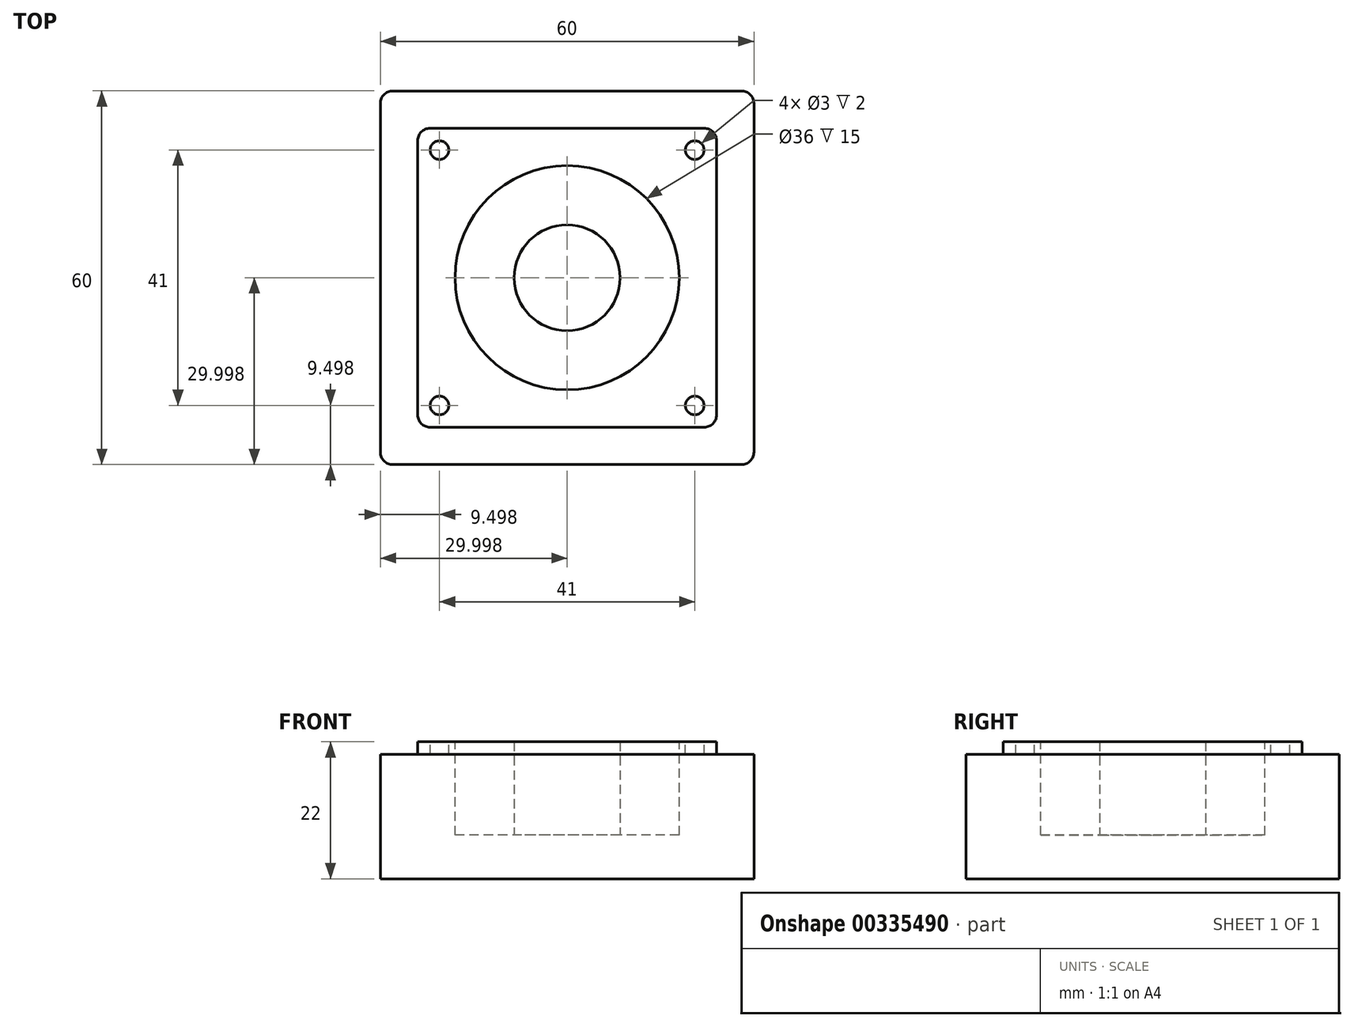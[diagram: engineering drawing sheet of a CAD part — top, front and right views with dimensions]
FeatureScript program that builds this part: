
annotation { "Feature Type Name" : "Feature", "Feature Type Description" : "" }
export const myFeature = defineFeature(function(context is Context, id is Id, definition is map)
    precondition{}
    {
        {
            var Q0;
            Q0=qCreatedBy(makeId("Top.planeOp"),FACE);
            var sketch = newSketch(context, id + "F0", { "sketchPlane" : qUnion([Q0])});
            skLineSegment(sketch, "E0.bottom", {"start": v(-15, 60.74) * mm, "end": v(45, 60.74) * mm});
            skLineSegment(sketch, "E0.top", {"start": v(-15, 0.74) * mm, "end": v(45, 0.74) * mm});
            skLineSegment(sketch, "E0.left", {"start": v(-15, 60.74) * mm, "end": v(-15, 0.74) * mm});
            skLineSegment(sketch, "E0.right", {"start": v(45, 60.74) * mm, "end": v(45, 0.74) * mm});
            skSolve(sketch);
        }
        {
            var Q0;
            Q0 = qSketchRegion(id + "F0", true);
            extrude(context, id + "F1", {"entities" : qUnion([Q0]), "depth" : 20 * mm});
        }
        {
            var Q0;
            Q0=makeQuery(id+"F1.opExtrude","CAP_FACE",FACE,{"disambiguationData":[OSD([sQuery(id+"F0.wireOp",EDGE,"E0.bottom"),sQuery(id+"F0.wireOp",EDGE,"E0.top"),sQuery(id+"F0.wireOp",EDGE,"E0.left"),sQuery(id+"F0.wireOp",EDGE,"E0.right")])],"isStart":false});
            var sketch = newSketch(context, id + "F2", { "sketchPlane" : qUnion([Q0])});
            skLineSegment(sketch, "E1.0", {"start": v(-9, 54.74) * mm, "end": v(-9, 6.74) * mm});
            skLineSegment(sketch, "E1.1", {"start": v(39, 54.74) * mm, "end": v(-9, 54.74) * mm});
            skLineSegment(sketch, "E1.2", {"start": v(39, 6.74) * mm, "end": v(39, 54.74) * mm});
            skLineSegment(sketch, "E1.3", {"start": v(-9, 6.74) * mm, "end": v(39, 6.74) * mm});
            skSolve(sketch);
        }
        {
            var Q0;
            Q0=makeQuery(id+"F2.imprint","IMPRINT",FACE,{"disambiguationData":[TD([[makeQuery(id+"F2.imprint","IMPRINT",EDGE,{"derivedFrom":sQuery(id+"F2.wireOp",EDGE,"E1.0")}),1.0]])]});
            extrude(context, id + "F3", {"entities" : qUnion([Q0]), "operationType" : NewBodyOperationType.ADD, "depth" : 2 * mm});
        }
        {
            var Q0;
            Q0=makeQuery(id+"F3.opExtrude","CAP_FACE",FACE,{"disambiguationData":[OSD([sQuery(id+"F2.wireOp",EDGE,"E1.0"),sQuery(id+"F2.wireOp",EDGE,"E1.1"),sQuery(id+"F2.wireOp",EDGE,"E1.2"),sQuery(id+"F2.wireOp",EDGE,"E1.3")])],"isStart":false});
            var sketch = newSketch(context, id + "F4", { "sketchPlane" : qUnion([Q0])});
            skLineSegment(sketch, "E2.0", {"start": v(-5.5, 51.24) * mm, "end": v(-5.5, 10.24) * mm});
            skLineSegment(sketch, "E2.1", {"start": v(35.5, 51.24) * mm, "end": v(-5.5, 51.24) * mm});
            skLineSegment(sketch, "E2.2", {"start": v(35.5, 10.24) * mm, "end": v(35.5, 51.24) * mm});
            skLineSegment(sketch, "E2.3", {"start": v(-5.5, 10.24) * mm, "end": v(35.5, 10.24) * mm});
            skCircle(sketch, "E3", {"center": v(-5.5, 51.24) * mm, "radius": 1.5 * mm});
            skCircle(sketch, "E4", {"center": v(35.5, 51.24) * mm, "radius": 1.5 * mm});
            skCircle(sketch, "E5", {"center": v(35.5, 10.24) * mm, "radius": 1.5 * mm});
            skCircle(sketch, "E6", {"center": v(-5.5, 10.24) * mm, "radius": 1.5 * mm});
            skSolve(sketch);
        }
        {
            var Q0;
            {var subQ0=sQuery(id+"F4.wireOp",EDGE,"E2.1");var subQ1=sQuery(id+"F4.wireOp",EDGE,"E2.0");var subQ2=makeQuery(id+"F4.imprint","INTERSECT",VERTEX,{"derivedFrom":[subQ1,subQ0]});Q0=makeQuery(id+"F4.imprint","IMPRINT",FACE,{"disambiguationData":[TD([[makeQuery(id+"F4.imprint","IMPRINT",EDGE,{"disambiguationData":[TD([[subQ2,-1.0]])],"derivedFrom":subQ1}),-1.0]])]});}
            var Q1;
            {var subQ0=sQuery(id+"F4.wireOp",EDGE,"E2.1");var subQ1=sQuery(id+"F4.wireOp",EDGE,"E2.0");var subQ2=makeQuery(id+"F4.imprint","INTERSECT",VERTEX,{"derivedFrom":[subQ1,subQ0]});Q1=makeQuery(id+"F4.imprint","IMPRINT",FACE,{"disambiguationData":[TD([[makeQuery(id+"F4.imprint","IMPRINT",EDGE,{"disambiguationData":[TD([[subQ2,-1.0]])],"derivedFrom":subQ1}),1.0]])]});}
            var Q2;
            {var subQ0=sQuery(id+"F4.wireOp",EDGE,"E2.2");var subQ1=sQuery(id+"F4.wireOp",EDGE,"E2.1");var subQ2=makeQuery(id+"F4.imprint","INTERSECT",VERTEX,{"derivedFrom":[subQ1,subQ0]});Q2=makeQuery(id+"F4.imprint","IMPRINT",FACE,{"disambiguationData":[TD([[makeQuery(id+"F4.imprint","IMPRINT",EDGE,{"disambiguationData":[TD([[subQ2,-1.0]])],"derivedFrom":subQ1}),1.0]])]});}
            var Q3;
            {var subQ0=sQuery(id+"F4.wireOp",EDGE,"E2.3");var subQ1=sQuery(id+"F4.wireOp",EDGE,"E2.2");var subQ2=makeQuery(id+"F4.imprint","INTERSECT",VERTEX,{"derivedFrom":[subQ1,subQ0]});Q3=makeQuery(id+"F4.imprint","IMPRINT",FACE,{"disambiguationData":[TD([[makeQuery(id+"F4.imprint","IMPRINT",EDGE,{"disambiguationData":[TD([[subQ2,-1.0]])],"derivedFrom":subQ1}),1.0]])]});}
            var Q4;
            {var subQ0=sQuery(id+"F4.wireOp",EDGE,"E2.3");var subQ1=sQuery(id+"F4.wireOp",EDGE,"E2.0");var subQ2=makeQuery(id+"F4.imprint","INTERSECT",VERTEX,{"derivedFrom":[subQ1,subQ0]});Q4=makeQuery(id+"F4.imprint","IMPRINT",FACE,{"disambiguationData":[TD([[makeQuery(id+"F4.imprint","IMPRINT",EDGE,{"disambiguationData":[TD([[subQ2,1.0]])],"derivedFrom":subQ1}),1.0]])]});}
            var Q5;
            {var subQ0=sQuery(id+"F4.wireOp",EDGE,"E2.3");var subQ1=sQuery(id+"F4.wireOp",EDGE,"E2.0");var subQ2=makeQuery(id+"F4.imprint","INTERSECT",VERTEX,{"derivedFrom":[subQ1,subQ0]});Q5=makeQuery(id+"F4.imprint","IMPRINT",FACE,{"disambiguationData":[TD([[makeQuery(id+"F4.imprint","IMPRINT",EDGE,{"disambiguationData":[TD([[subQ2,1.0]])],"derivedFrom":subQ1}),-1.0]])]});}
            var Q6;
            {var subQ0=sQuery(id+"F4.wireOp",EDGE,"E2.3");var subQ1=sQuery(id+"F4.wireOp",EDGE,"E2.2");var subQ2=makeQuery(id+"F4.imprint","INTERSECT",VERTEX,{"derivedFrom":[subQ1,subQ0]});Q6=makeQuery(id+"F4.imprint","IMPRINT",FACE,{"disambiguationData":[TD([[makeQuery(id+"F4.imprint","IMPRINT",EDGE,{"disambiguationData":[TD([[subQ2,-1.0]])],"derivedFrom":subQ1}),-1.0]])]});}
            var Q7;
            {var subQ0=sQuery(id+"F4.wireOp",EDGE,"E2.2");var subQ1=sQuery(id+"F4.wireOp",EDGE,"E2.1");var subQ2=makeQuery(id+"F4.imprint","INTERSECT",VERTEX,{"derivedFrom":[subQ1,subQ0]});Q7=makeQuery(id+"F4.imprint","IMPRINT",FACE,{"disambiguationData":[TD([[makeQuery(id+"F4.imprint","IMPRINT",EDGE,{"disambiguationData":[TD([[subQ2,-1.0]])],"derivedFrom":subQ1}),-1.0]])]});}
            extrude(context, id + "F5", {"entities" : qUnion([Q0, Q1, Q2, Q3, Q4, Q5, Q6, Q7]), "operationType" : NewBodyOperationType.REMOVE, "oppositeDirection" : true, "depth" : 2 * mm});
        }
        {
            var Q0;
            Q0=makeQuery(id+"F3.opExtrude","CAP_FACE",FACE,{"disambiguationData":[OSD([sQuery(id+"F2.wireOp",EDGE,"E1.0"),sQuery(id+"F2.wireOp",EDGE,"E1.1"),sQuery(id+"F2.wireOp",EDGE,"E1.2"),sQuery(id+"F2.wireOp",EDGE,"E1.3")])],"isStart":false});
            var sketch = newSketch(context, id + "F6", { "sketchPlane" : qUnion([Q0])});
            skCircle(sketch, "E7", {"center": v(15, 30.74) * mm, "radius": 18 * mm});
            skPoint(sketch, "E7.centerSnap0", {"position": v(39, 30.74) * mm});
            skPoint(sketch, "E7.centerSnap1", {"position": v(15, 54.74) * mm});
            skSolve(sketch);
        }
        {
            var Q0;
            Q0=makeQuery(id+"F6.imprint","IMPRINT",FACE,{"disambiguationData":[TD([[makeQuery(id+"F6.imprint","IMPRINT",EDGE,{"derivedFrom":sQuery(id+"F6.wireOp",EDGE,"E7")}),1.0]])]});
            extrude(context, id + "F7", {"entities" : qUnion([Q0]), "operationType" : NewBodyOperationType.REMOVE, "oppositeDirection" : true, "depth" : 15 * mm});
        }
        {
            var Q0;
            Q0=makeQuery(id+"F7.boolean.opBoolean","COPY",FACE,{"derivedFrom":makeQuery(id+"F7.opExtrude","CAP_FACE",FACE,{"disambiguationData":[OSD([sQuery(id+"F6.wireOp",EDGE,"E7")])],"isStart":false})});
            var sketch = newSketch(context, id + "F8", { "sketchPlane" : qUnion([Q0])});
            skCircle(sketch, "E8", {"center": v(15, 30.74) * mm, "radius": 8.5 * mm});
            skSolve(sketch);
        }
        {
            var Q0;
            Q0 = qSketchRegion(id + "F8", true);
            extrude(context, id + "F9", {"entities" : qUnion([Q0]), "operationType" : NewBodyOperationType.ADD, "depth" : 15 * mm});
        }
        {
            var Q0;
            Q0=makeQuery(id+"F1.opExtrude","SWEPT_EDGE",EDGE,{"disambiguationData":[OSD([sQuery(id+"F0.wireOp",EDGE,"E0.bottom"),sQuery(id+"F0.wireOp",EDGE,"E0.right")])]});
            var Q1;
            Q1=makeQuery(id+"F1.opExtrude","SWEPT_EDGE",EDGE,{"disambiguationData":[OSD([sQuery(id+"F0.wireOp",EDGE,"E0.top"),sQuery(id+"F0.wireOp",EDGE,"E0.right")])]});
            var Q2;
            Q2=makeQuery(id+"F1.opExtrude","SWEPT_EDGE",EDGE,{"disambiguationData":[OSD([sQuery(id+"F0.wireOp",EDGE,"E0.top"),sQuery(id+"F0.wireOp",EDGE,"E0.left")])]});
            var Q3;
            Q3=makeQuery(id+"F1.opExtrude","SWEPT_EDGE",EDGE,{"disambiguationData":[OSD([sQuery(id+"F0.wireOp",EDGE,"E0.bottom"),sQuery(id+"F0.wireOp",EDGE,"E0.left")])]});
            var Q4;
            Q4=makeQuery(id+"F3.opExtrude","SWEPT_EDGE",EDGE,{"disambiguationData":[OSD([sQuery(id+"F2.wireOp",EDGE,"E1.0"),sQuery(id+"F2.wireOp",EDGE,"E1.1")])]});
            var Q5;
            Q5=makeQuery(id+"F3.opExtrude","SWEPT_EDGE",EDGE,{"disambiguationData":[OSD([sQuery(id+"F2.wireOp",EDGE,"E1.0"),sQuery(id+"F2.wireOp",EDGE,"E1.3")])]});
            var Q6;
            Q6=makeQuery(id+"F3.opExtrude","SWEPT_EDGE",EDGE,{"disambiguationData":[OSD([sQuery(id+"F2.wireOp",EDGE,"E1.2"),sQuery(id+"F2.wireOp",EDGE,"E1.3")])]});
            var Q7;
            Q7=makeQuery(id+"F3.opExtrude","SWEPT_EDGE",EDGE,{"disambiguationData":[OSD([sQuery(id+"F2.wireOp",EDGE,"E1.1"),sQuery(id+"F2.wireOp",EDGE,"E1.2")])]});
            fillet(context, id + "F10", {"entities" : qUnion([Q0, Q1, Q2, Q3, Q4, Q5, Q6, Q7]), "radius" : 2 * mm, "tangentPropagation" : true, "allowEdgeOverflow" : false});
        }
    });
